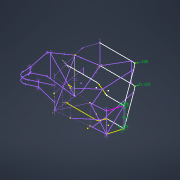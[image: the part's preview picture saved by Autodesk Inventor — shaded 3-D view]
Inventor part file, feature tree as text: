
AUTODESK INVENTOR PART (.ipt)
format: ipt  version: 2022 (Build 260153000, 153)  size: 224,256 bytes
history: native  units: mm
features: other x18, sketch x5, plane x2
ambient origin geometry x8: Origin, YZ Plane, XZ Plane, XY Plane, X Axis, Y Axis, Z Axis, Center Point
feature tree (25):
  other  "Assoalho"
  other  "Plano de trabalho2"
  other  "Plano de trabalho6"
  other  "Plano de trabalho7"
  other  "Plano de trabalho9"
  other  "angulo de ataque"
  other  "FAB SUSP"
  other  "plano do tanque"
  other  "plano fire"
  other  "Firewall"
  other  "Posição eixo final"
  other  "TRASEIRA"
  other  "OSIM"
  other  "Boneco De M"
  other  "ref0"
  other  "ref1"
  other  "Plano de trabalho15"
  plane  "Work Plane21"
  other  "SIM"
  sketch  "Sketch30"  dims[d10=290.0mm d42=32.114058mm]
  plane  "Work Plane23"
  sketch  "Sketch31"  dims[d117=318.406mm]
  sketch  "3D Sketch15"
  sketch  "Esboço32"  dims[d118=318.406mm d133=160.0mm d141=13.788101mm d169=800.0mm d170=500.0mm d171=490.0mm d172=600.0mm d175=15.400159mm d178=330.0mm d179=10.754719mm d180=310.0mm d181=20.071286mm d182=23.88704mm d183=549.790416mm d188=570.0mm d189=10.0mm d190=25.0mm d225=120.0mm d236=15.7mm d302=280.0mm d303=60.0mm d305=770.0mm d307=120.0mm d309=110.0mm d310=110.0mm d311=105.0mm d312=105.0mm d313=0.0mm d317=105.0mm d318=15.0mm d320=100.0mm d321=90.0mm d322=90.0mm d323=200.0mm d324=200.0mm d326=416.0mm d327=105.0mm d328=105.0mm d329=4.269mm d330=4.269mm d332=20.0mm d333=20.0mm d334=20.0mm d335=20.0mm]
  sketch  "Esboço 3D16"  dims[d5=175.0mm]
